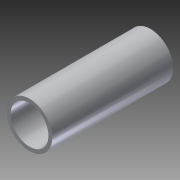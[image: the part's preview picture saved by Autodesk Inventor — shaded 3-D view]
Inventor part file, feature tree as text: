
AUTODESK INVENTOR PART (.ipt)
format: ipt  version: 2013 (Build 170138000, 138)  size: 84,480 bytes
history: native  units: in
note: dims shown in document units (in); Inventor stores cm internally (conversion verified against a paired STEP export)
features: extrude x1, sketch x1
ambient origin geometry x8: Origin, YZ Plane, XZ Plane, XY Plane, X Axis, Y Axis, Z Axis, Center Point
bodies: Solid1 (feature_tree)
feature tree (2):
  extrude  "Extrusion1"  Depth=0.625in
  sketch  "Sketch1"  dims[d0=0.75in d1=0.625in d2=2.0in d3=0.0in]
